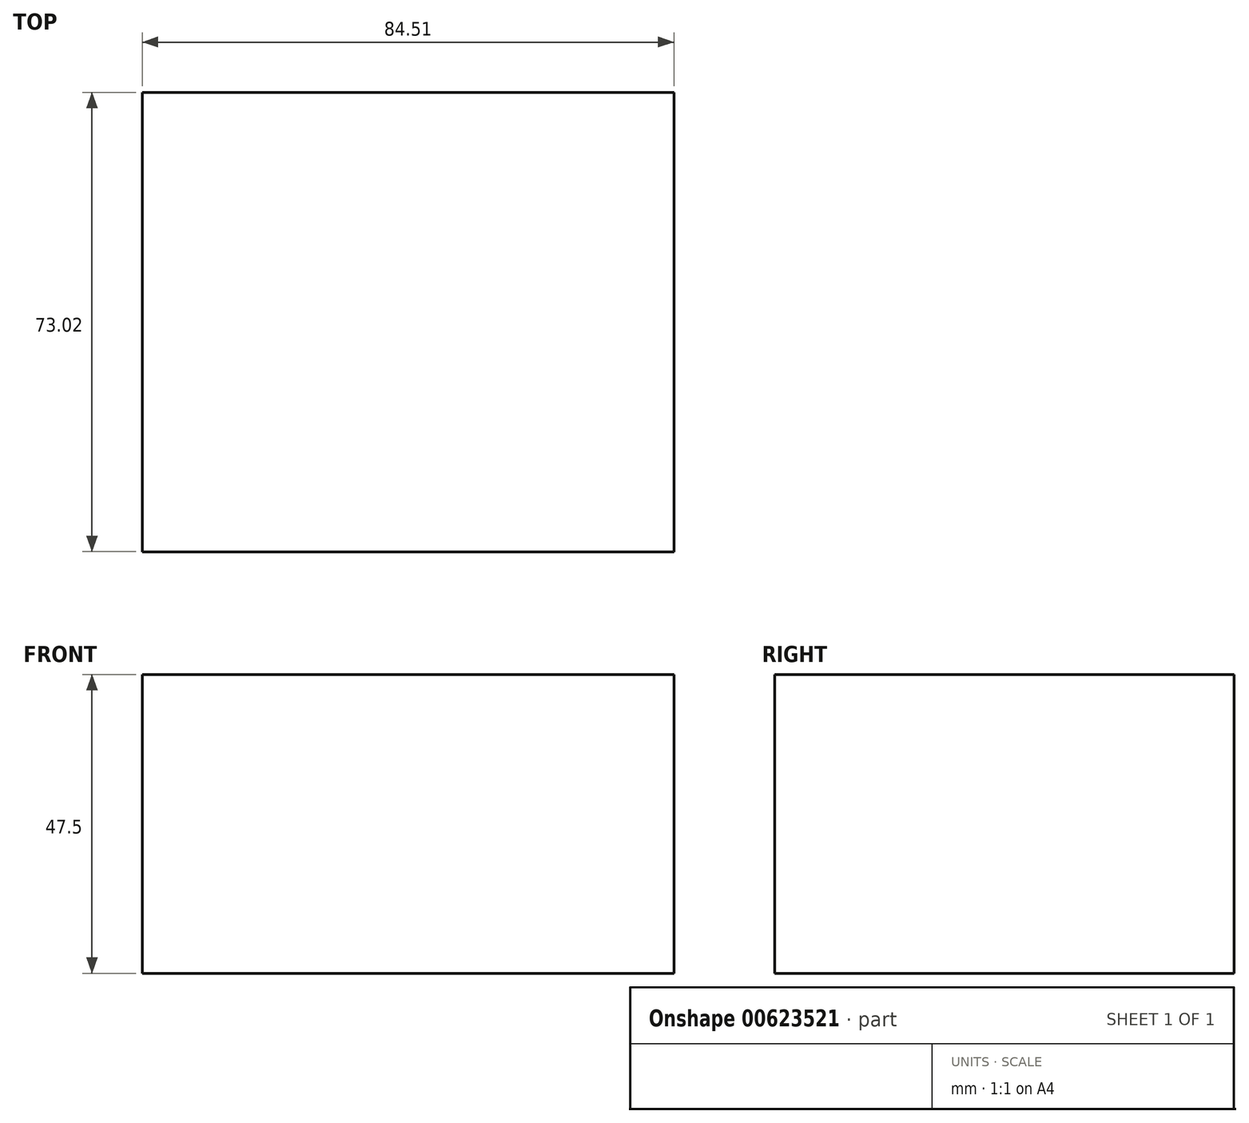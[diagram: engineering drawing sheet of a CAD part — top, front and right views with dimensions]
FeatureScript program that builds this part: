
annotation { "Feature Type Name" : "Feature", "Feature Type Description" : "" }
export const myFeature = defineFeature(function(context is Context, id is Id, definition is map)
    precondition{}
    {
        {
            var Q0;
            Q0=qCreatedBy(makeId("Top.planeOp"),FACE);
            var sketch = newSketch(context, id + "F0", { "sketchPlane" : qUnion([Q0])});
            skLineSegment(sketch, "E0.bottom", {"start": v(-54.91, -53.85) * mm, "end": v(29.6, -53.85) * mm});
            skLineSegment(sketch, "E0.top", {"start": v(-54.91, 19.17) * mm, "end": v(29.6, 19.17) * mm});
            skLineSegment(sketch, "E0.left", {"start": v(-54.91, -53.85) * mm, "end": v(-54.91, 19.17) * mm});
            skLineSegment(sketch, "E0.right", {"start": v(29.6, -53.85) * mm, "end": v(29.6, 19.17) * mm});
            skSolve(sketch);
        }
        {
            var Q0;
            Q0=makeQuery(id+"F0.imprint","IMPRINT",FACE,{"disambiguationData":[TD([[makeQuery(id+"F0.imprint","IMPRINT",EDGE,{"derivedFrom":sQuery(id+"F0.wireOp",EDGE,"E0.bottom")}),1.0]])]});
            extrude(context, id + "F1", {"entities" : qUnion([Q0]), "depth" : 47.5 * mm, "offsetDistance" : 25.4 * mm});
        }
    });
